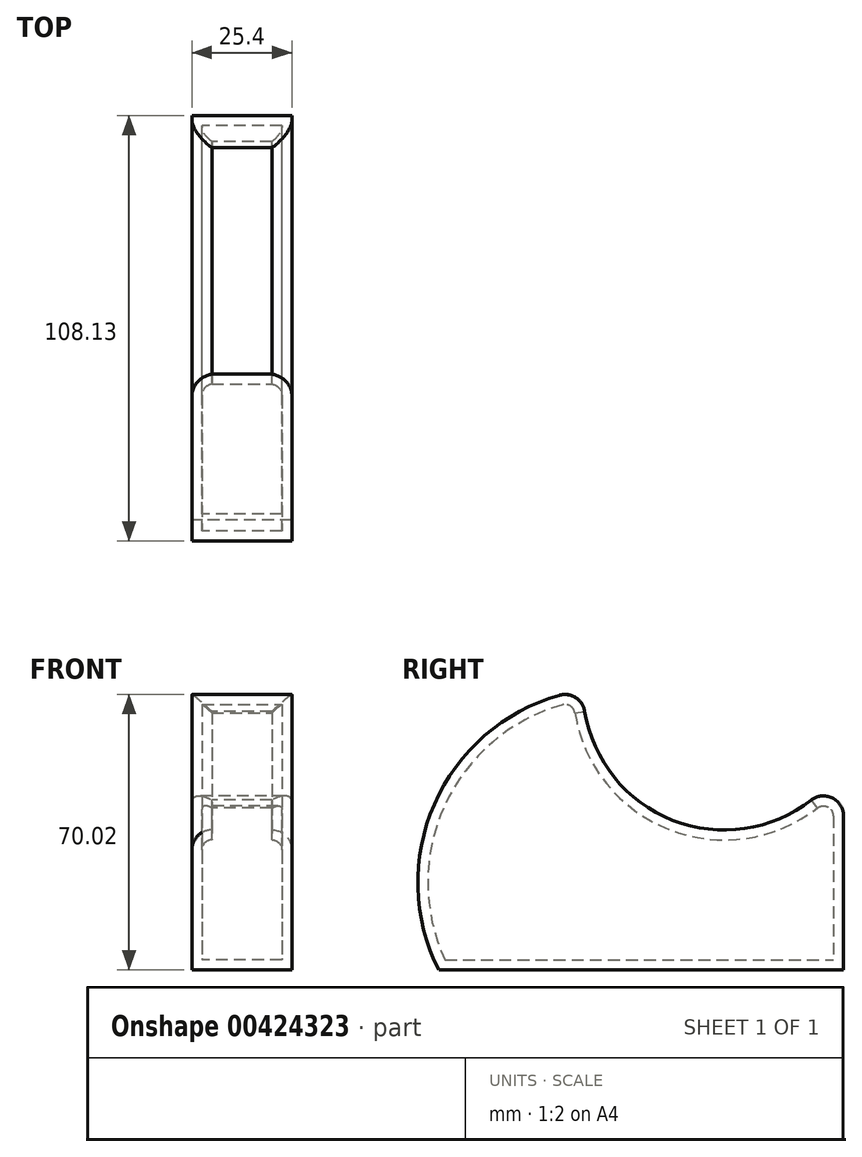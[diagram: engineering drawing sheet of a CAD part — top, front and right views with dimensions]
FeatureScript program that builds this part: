
annotation { "Feature Type Name" : "Feature", "Feature Type Description" : "" }
export const myFeature = defineFeature(function(context is Context, id is Id, definition is map)
    precondition{}
    {
        {
            var Q0;
            Q0=qCreatedBy(makeId("Right.planeOp"),FACE);
            var sketch = newSketch(context, id + "F0", { "sketchPlane" : qUnion([Q0])});
            skLineSegment(sketch, "E0", {"start": v(-43.4, -52.18) * mm, "end": v(59.42, -52.18) * mm});
            skArc(sketch, "E1", {"start": v(-6.8, 18.94) * mm, "mid": v(-43.23, -7.29) * mm, "end": v(-43.4, -52.18) * mm});
            skArc(sketch, "E2", {"start": v(-6.8, 18.94) * mm, "mid": v(19.26, -15.19) * mm, "end": v(59.42, 0) * mm});
            skLineSegment(sketch, "E3", {"start": v(59.42, 0) * mm, "end": v(59.42, -52.18) * mm});
            skSolve(sketch);
        }
        {
            var Q0;
            Q0 = qSketchRegion(id + "F0", true);
            extrude(context, id + "F1", {"entities" : qUnion([Q0]), "depth" : 25.4 * mm});
        }
        {
            var Q0;
            Q0=makeQuery(id+"F1.opExtrude","SWEPT_FACE",FACE,{"disambiguationData":[OSD([sQuery(id+"F0.wireOp",EDGE,"E2")])]});
            fillet(context, id + "F2", {"entities" : qUnion([Q0]), "radius" : 5.08 * mm, "tangentPropagation" : true, "allowEdgeOverflow" : false});
        }
        {
            var Q0;
            Q0=makeQuery(id+"F1.opExtrude","SWEPT_FACE",FACE,{"disambiguationData":[OSD([sQuery(id+"F0.wireOp",EDGE,"E2")])]});
            shell(context, id + "F3", {"entities" : qUnion([Q0]), "thickness" : 2.54 * mm});
        }
    });
